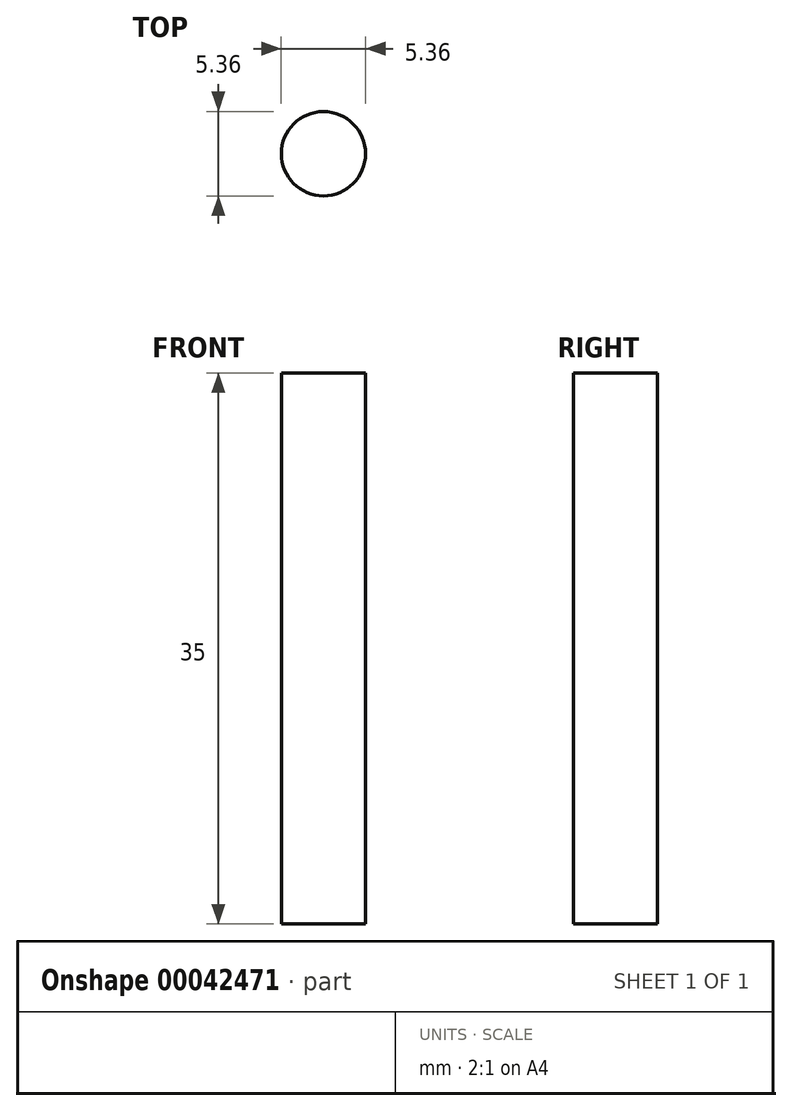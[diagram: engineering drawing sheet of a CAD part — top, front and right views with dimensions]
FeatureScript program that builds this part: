
annotation { "Feature Type Name" : "Feature", "Feature Type Description" : "" }
export const myFeature = defineFeature(function(context is Context, id is Id, definition is map)
    precondition{}
    {
        {
            var Q0;
            Q0=qCreatedBy(makeId("Top.planeOp"),FACE);
            var sketch = newSketch(context, id + "F0", { "sketchPlane" : qUnion([Q0])});
            skCircle(sketch, "E0", {"center": v(0, 0) * mm, "radius": 2.68 * mm});
            skSolve(sketch);
        }
        {
            var Q0;
            Q0 = qSketchRegion(id + "F0", true);
            extrude(context, id + "F1", {"entities" : qUnion([Q0]), "depth" : 35 * mm});
        }
    });
